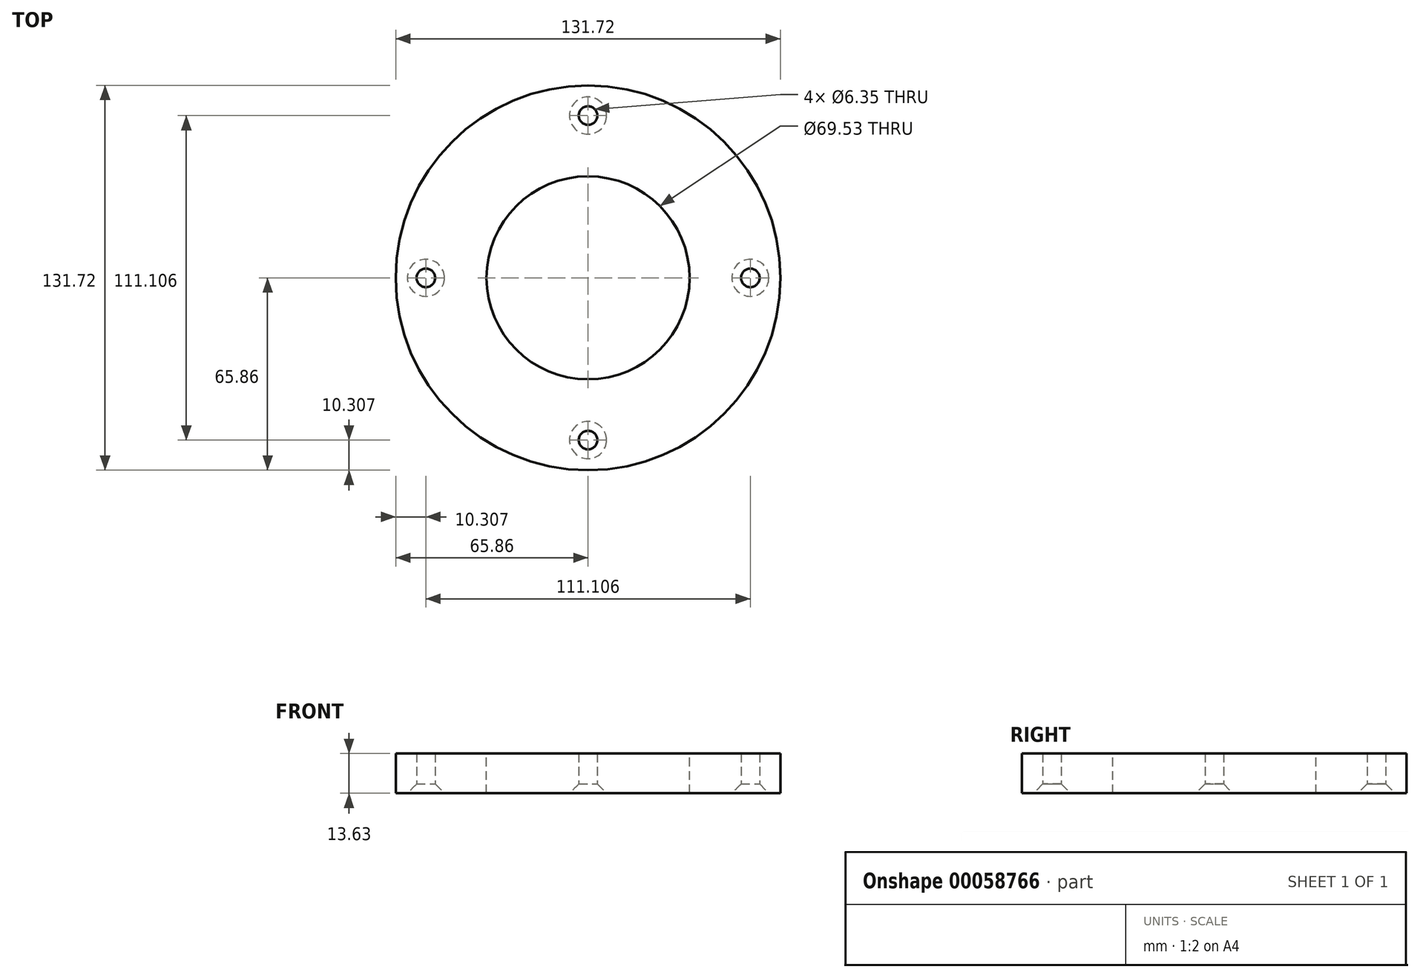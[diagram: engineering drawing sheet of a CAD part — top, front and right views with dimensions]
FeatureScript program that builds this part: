
annotation { "Feature Type Name" : "Feature", "Feature Type Description" : "" }
export const myFeature = defineFeature(function(context is Context, id is Id, definition is map)
    precondition{}
    {
        {
            var Q0;
            Q0=qCreatedBy(makeId("Front.planeOp"),FACE);
            var sketch = newSketch(context, id + "F0", { "sketchPlane" : qUnion([Q0])});
            skLineSegment(sketch, "E0.bottom", {"start": v(-65.86, 13.63) * mm, "end": v(-34.76, 13.63) * mm});
            skLineSegment(sketch, "E0.top", {"start": v(-65.86, 0) * mm, "end": v(-34.76, 0) * mm});
            skLineSegment(sketch, "E0.left", {"start": v(-65.86, 13.63) * mm, "end": v(-65.86, 0) * mm});
            skLineSegment(sketch, "E0.right", {"start": v(-34.76, 13.63) * mm, "end": v(-34.76, 0) * mm});
            skLineSegment(sketch, "E1", {"start": v(0, 44.72) * mm, "end": v(0, -54.85) * mm});
            skSolve(sketch);
        }
        {
            var Q0;
            Q0=makeQuery(id+"F0.imprint","IMPRINT",FACE,{"disambiguationData":[TD([[makeQuery(id+"F0.imprint","IMPRINT",EDGE,{"derivedFrom":sQuery(id+"F0.wireOp",EDGE,"E0.bottom")}),-1.0]])]});
            var Q1;
            Q1=sQuery(id+"F0.wireOp",EDGE,"E1");
            revolve(context, id + "F1", {"entities" : qUnion([Q0]), "axis" : qUnion([Q1]), "revolveType" : RevolveType.FULL});
        }
        {
            var Q0;
            Q0=qCreatedBy(makeId("Top.planeOp"),FACE);
            var sketch = newSketch(context, id + "F2", { "sketchPlane" : qUnion([Q0])});
            skCircle(sketch, "E2", {"center": v(0, 0) * mm, "radius": 55.55 * mm});
            skCircle(sketch, "E3", {"center": v(0, 55.55) * mm, "radius": 6.94 * mm});
            skCircle(sketch, "E4", {"center": v(55.55, 0) * mm, "radius": 6.94 * mm});
            skCircle(sketch, "E5", {"center": v(0, -55.55) * mm, "radius": 6.94 * mm});
            skCircle(sketch, "E6", {"center": v(-55.55, 0) * mm, "radius": 6.94 * mm});
            skLineSegment(sketch, "E7", {"start": v(0, -66.03) * mm, "end": v(0, -45.07) * mm});
            skSolve(sketch);
        }
        {
            var Q0;
            Q0=sQuery(id+"F2.wireOp",VERTEX,"E4.center");
            var Q1;
            Q1=sQuery(id+"F2.wireOp",VERTEX,"E3.center");
            var Q2;
            Q2=sQuery(id+"F2.wireOp",VERTEX,"E6.center");
            var Q3;
            Q3=sQuery(id+"F2.wireOp",VERTEX,"E5.center");
            var Q4;
            Q4=makeQuery(id+"F1.opRevolve","SWEPT_BODY",BODY,{"disambiguationData":[OSD([sQuery(id+"F0.wireOp",EDGE,"E0.bottom"),sQuery(id+"F0.wireOp",EDGE,"E0.top"),sQuery(id+"F0.wireOp",EDGE,"E0.left"),sQuery(id+"F0.wireOp",EDGE,"E0.right")])]});
            hole(context, id + "F3", {"style" : HoleStyle.C_SINK, "holeDiameter" : 6.35 * mm, "cSinkDiameter" : 12.7 * mm, "endStyle" : HoleEndStyle.THROUGH, "oppositeDirection" : true, "locations" : qUnion([Q0, Q1, Q2, Q3]), "scope" : qUnion([Q4]), "cSinkAngle" : 90 * degree});
        }
    });
